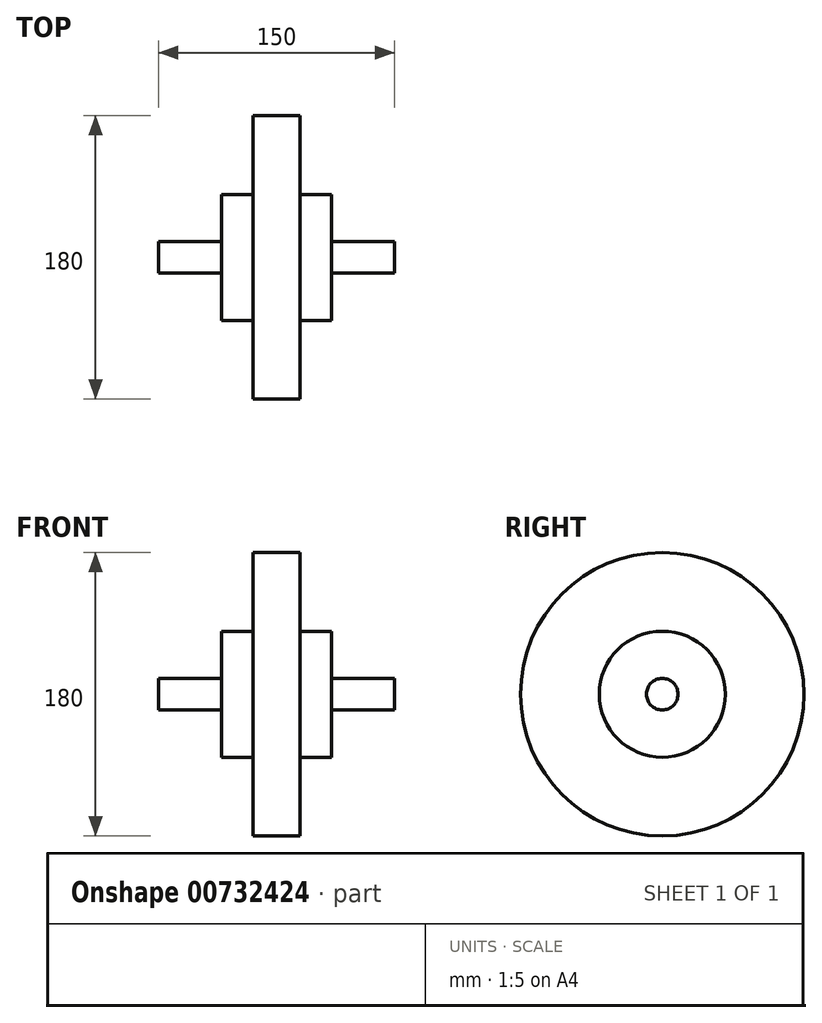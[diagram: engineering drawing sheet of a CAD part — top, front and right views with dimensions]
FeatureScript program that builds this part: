
annotation { "Feature Type Name" : "Feature", "Feature Type Description" : "" }
export const myFeature = defineFeature(function(context is Context, id is Id, definition is map)
    precondition{}
    {
        {
            var Q0;
            Q0=qCreatedBy(makeId("Front.planeOp"),FACE);
            var sketch = newSketch(context, id + "F0", { "sketchPlane" : qUnion([Q0])});
            skLineSegment(sketch, "E0", {"start": v(-150, 0) * mm, "end": v(-110, 0) * mm});
            skLineSegment(sketch, "E1", {"start": v(-110, 0) * mm, "end": v(-110, 30) * mm});
            skLineSegment(sketch, "E2", {"start": v(-110, 30) * mm, "end": v(-90, 30) * mm});
            skLineSegment(sketch, "E3", {"start": v(-90, 30) * mm, "end": v(-90, 80) * mm});
            skLineSegment(sketch, "E4", {"start": v(-90, 80) * mm, "end": v(-60, 80) * mm});
            skLineSegment(sketch, "E5", {"start": v(-60, 80) * mm, "end": v(-60, 30) * mm});
            skLineSegment(sketch, "E6", {"start": v(-60, 30) * mm, "end": v(-40, 30) * mm});
            skLineSegment(sketch, "E7", {"start": v(-40, 30) * mm, "end": v(-40, 0) * mm});
            skLineSegment(sketch, "E8", {"start": v(-40, 0) * mm, "end": v(0, 0) * mm});
            skLineSegment(sketch, "E9", {"start": v(0, 0) * mm, "end": v(0, -10) * mm});
            skLineSegment(sketch, "E10", {"start": v(-150, -10) * mm, "end": v(-150, 0) * mm});
            skLineSegment(sketch, "E11", {"start": v(0, -10) * mm, "end": v(-150, -10) * mm});
            skSolve(sketch);
        }
        {
            var Q0;
            Q0=makeQuery(id+"F0.imprint","IMPRINT",FACE,{"disambiguationData":[TD([[makeQuery(id+"F0.imprint","IMPRINT",EDGE,{"derivedFrom":sQuery(id+"F0.wireOp",EDGE,"E0")}),-1.0]])]});
            var Q1;
            Q1=sQuery(id+"F0.wireOp",EDGE,"E11");
            revolve(context, id + "F1", {"surfaceOperationType" : NewSurfaceOperationType.NEW, "entities" : qUnion([Q0]), "axis" : qUnion([Q1]), "revolveType" : RevolveType.FULL});
        }
    });
